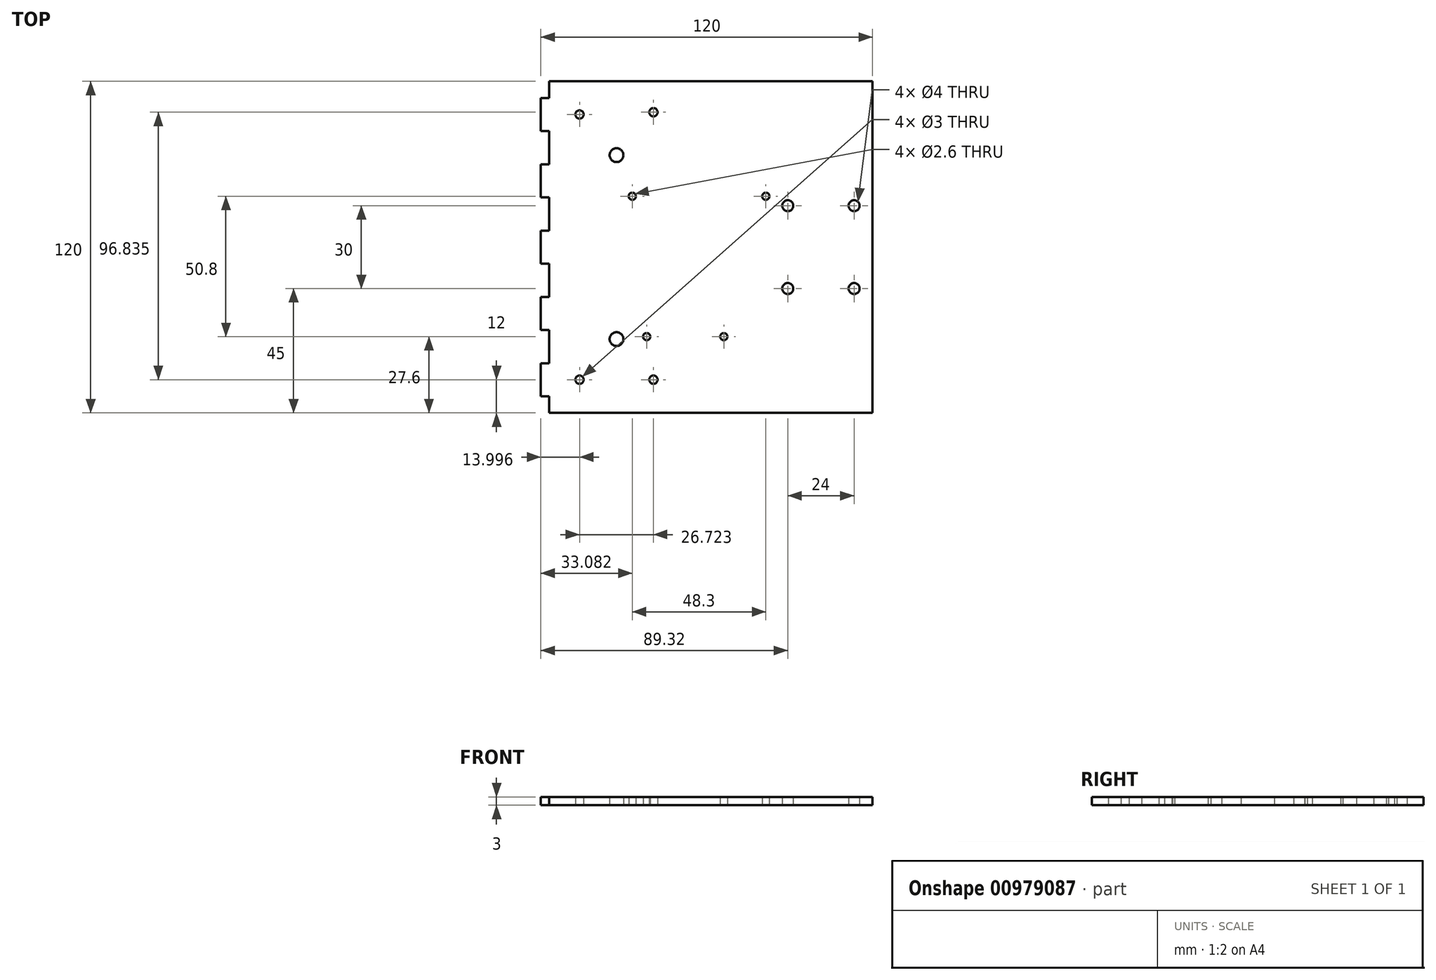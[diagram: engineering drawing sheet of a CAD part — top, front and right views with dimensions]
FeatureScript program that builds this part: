
annotation { "Feature Type Name" : "Feature", "Feature Type Description" : "" }
export const myFeature = defineFeature(function(context is Context, id is Id, definition is map)
    precondition{}
    {
        {
            var Q0;
            Q0=qCreatedBy(makeId("Top.planeOp"),FACE);
            var sketch = newSketch(context, id + "F0", { "sketchPlane" : qUnion([Q0])});
            skLineSegment(sketch, "E0.bottom", {"start": v(74.5, 60) * mm, "end": v(-42.5, 60) * mm});
            skLineSegment(sketch, "E0.top", {"start": v(74.5, -60) * mm, "end": v(-42.5, -60) * mm});
            skLineSegment(sketch, "E0.left", {"start": v(74.5, 60) * mm, "end": v(74.5, -60) * mm});
            skPoint(sketch, "E0.middle", {"position": v(18.5, -7) * mm});
            skCircle(sketch, "E1", {"center": v(-4.77, 48.84) * mm, "radius": 1.5 * mm});
            skCircle(sketch, "E2.MirrorC", {"center": v(-31.5, 48) * mm, "radius": 1.5 * mm});
            skCircle(sketch, "E3.MirrorC", {"center": v(-31.5, -48) * mm, "radius": 1.5 * mm});
            skCircle(sketch, "E4.MirrorC", {"center": v(-4.77, -48) * mm, "radius": 1.5 * mm});
            skLineSegment(sketch, "E5", {"start": v(-31.5, -48) * mm, "end": v(-4.77, -48) * mm});
            skLineSegment(sketch, "E6", {"start": v(-18.13, -48) * mm, "end": v(-18.12, -27.1) * mm});
            skCircle(sketch, "E7", {"center": v(-18.12, -33.29) * mm, "radius": 2.5 * mm});
            skPoint(sketch, "E8.endSnap0", {"position": v(-45.5, 0) * mm});
            skCircle(sketch, "E9.MirrorC", {"center": v(-18.12, 33.29) * mm, "radius": 2.5 * mm});
            skPoint(sketch, "E10.visualSharp", {"position": v(74.5, 60) * mm});
            skLineSegment(sketch, "E10.filletArc", {"start": v(74.5, 60) * mm, "end": v(74.5, 60) * mm});
            skPoint(sketch, "E11.visualSharp", {"position": v(74.5, -60) * mm});
            skLineSegment(sketch, "E11.filletArc", {"start": v(74.5, -60) * mm, "end": v(74.5, -60) * mm});
            skLineSegment(sketch, "E12", {"start": v(74.5, 0) * mm, "end": v(25.27, 0) * mm});
            skCircle(sketch, "E13", {"center": v(67.83, 15) * mm, "radius": 2 * mm});
            skCircle(sketch, "E14", {"center": v(43.83, 15) * mm, "radius": 2 * mm});
            skCircle(sketch, "E15.MirrorC", {"center": v(67.83, -15) * mm, "radius": 2 * mm});
            skCircle(sketch, "E16.MirrorC", {"center": v(43.83, -15) * mm, "radius": 2 * mm});
            skLineSegment(sketch, "E17.bottom", {"start": v(35.9, 18.4) * mm, "end": v(-12.4, 18.4) * mm});
            skLineSegment(sketch, "E17.top", {"start": v(35.9, -32.4) * mm, "end": v(-12.4, -32.4) * mm});
            skLineSegment(sketch, "E17.left", {"start": v(35.9, 18.4) * mm, "end": v(35.9, -32.4) * mm});
            skLineSegment(sketch, "E17.right", {"start": v(-12.4, 18.4) * mm, "end": v(-12.4, -32.4) * mm});
            skPoint(sketch, "E17.middle", {"position": v(11.74, -7) * mm});
            skCircle(sketch, "E18", {"center": v(35.9, 18.4) * mm, "radius": 1.3 * mm});
            skCircle(sketch, "E19", {"center": v(-12.4, 18.4) * mm, "radius": 1.3 * mm});
            skCircle(sketch, "E20", {"center": v(20.7, -32.4) * mm, "radius": 1.3 * mm});
            skCircle(sketch, "E21", {"center": v(-7.2, -32.4) * mm, "radius": 1.3 * mm});
            skLineSegment(sketch, "E22.left", {"start": v(-42.5, -6) * mm, "end": v(-45.5, -6) * mm});
            skLineSegment(sketch, "E22.right", {"start": v(-42.5, 6) * mm, "end": v(-45.5, 6) * mm});
            skLineSegment(sketch, "E23.1.0.0", {"start": v(-42.5, -30) * mm, "end": v(-45.5, -30) * mm});
            skLineSegment(sketch, "E23.1.0.1", {"start": v(-42.5, -18) * mm, "end": v(-45.5, -18) * mm});
            skLineSegment(sketch, "E23.2.0.0", {"start": v(-42.5, -54) * mm, "end": v(-45.5, -54) * mm});
            skLineSegment(sketch, "E23.2.0.1", {"start": v(-42.5, -42) * mm, "end": v(-45.5, -42) * mm});
            skLineSegment(sketch, "E24.1.0.1", {"start": v(-42.5, 30) * mm, "end": v(-45.5, 30) * mm});
            skLineSegment(sketch, "E24.1.0.3", {"start": v(-42.5, 18) * mm, "end": v(-45.5, 18) * mm});
            skLineSegment(sketch, "E24.2.0.1", {"start": v(-42.5, 54) * mm, "end": v(-45.5, 54) * mm});
            skLineSegment(sketch, "E24.2.0.3", {"start": v(-42.5, 42) * mm, "end": v(-45.5, 42) * mm});
            skLineSegment(sketch, "E25", {"start": v(-42.5, 60) * mm, "end": v(-42.5, 54) * mm});
            skLineSegment(sketch, "E26", {"start": v(-45.5, -54) * mm, "end": v(-45.5, -42) * mm});
            skLineSegment(sketch, "E27.trimOffspring", {"start": v(-42.5, 42) * mm, "end": v(-42.5, 30) * mm});
            skLineSegment(sketch, "E28.trimOffspring", {"start": v(-45.5, 42) * mm, "end": v(-45.5, 54) * mm});
            skLineSegment(sketch, "E29.trimOffspring", {"start": v(-42.5, 18) * mm, "end": v(-42.5, 6) * mm});
            skLineSegment(sketch, "E30.trimOffspring", {"start": v(-45.5, 18) * mm, "end": v(-45.5, 30) * mm});
            skLineSegment(sketch, "E31.trimOffspring", {"start": v(-42.5, -6) * mm, "end": v(-42.5, -18) * mm});
            skLineSegment(sketch, "E32.trimOffspring", {"start": v(-45.5, -6) * mm, "end": v(-45.5, 6) * mm});
            skLineSegment(sketch, "E33.trimOffspring", {"start": v(-42.5, -30) * mm, "end": v(-42.5, -42) * mm});
            skLineSegment(sketch, "E34.trimOffspring", {"start": v(-45.5, -30) * mm, "end": v(-45.5, -18) * mm});
            skLineSegment(sketch, "E35.trimOffspring", {"start": v(-42.5, -54) * mm, "end": v(-42.5, -60) * mm});
            skSolve(sketch);
        }
        {
            var Q0;
            Q0 = qSketchRegion(id + "F0", true);
            var Q1;
            {var subQ7=sQuery(id+"F0.wireOp",EDGE,"E17.left");var subQ10=makeQuery(id+"F0.imprint","IMPRINT",VERTEX,{"derivedFrom":subQ7});Q1=makeQuery(id+"F0.imprint","IMPRINT",FACE,{"disambiguationData":[TD([[makeQuery(id+"F0.imprint","IMPRINT",EDGE,{"disambiguationData":[TD([[subQ10,1.0]])],"derivedFrom":subQ7}),-1.0]])]});}
            extrude(context, id + "F1", {"entities" : qUnion([Q0, Q1]), "depth" : 3 * mm, "offsetDistance" : 25 * mm});
        }
    });
